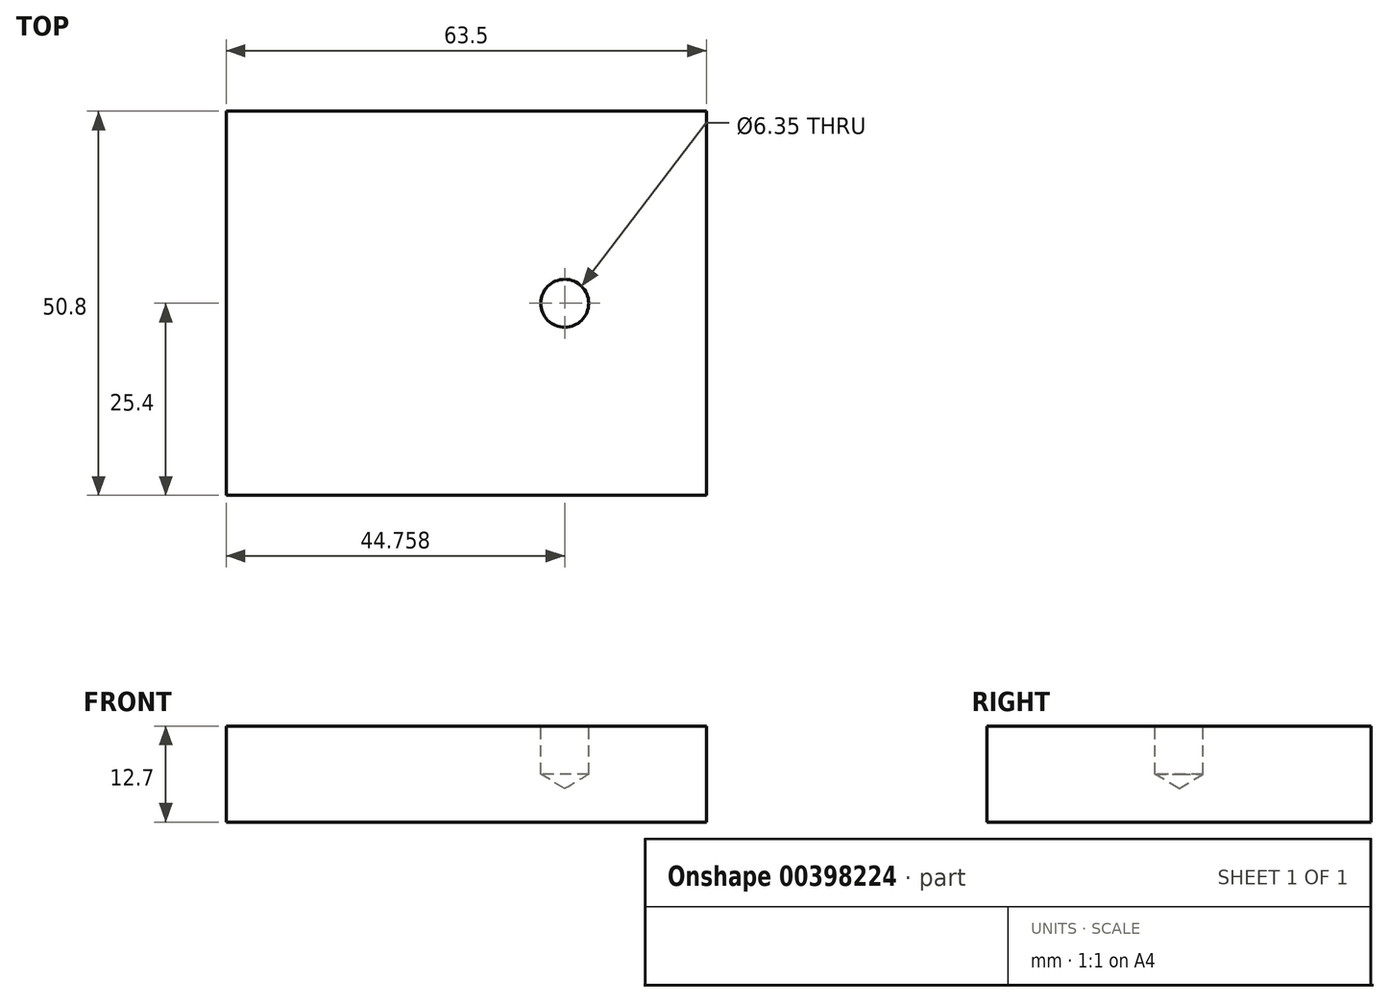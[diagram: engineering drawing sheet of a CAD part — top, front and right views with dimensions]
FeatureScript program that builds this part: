
annotation { "Feature Type Name" : "Feature", "Feature Type Description" : "" }
export const myFeature = defineFeature(function(context is Context, id is Id, definition is map)
    precondition{}
    {
        {
            var Q0;
            Q0=qCreatedBy(makeId("Top.planeOp"),FACE);
            var sketch = newSketch(context, id + "F0", { "sketchPlane" : qUnion([Q0])});
            skLineSegment(sketch, "E0.bottom", {"start": v(-31.75, 25.4) * mm, "end": v(31.75, 25.4) * mm});
            skLineSegment(sketch, "E0.top", {"start": v(-31.75, -25.4) * mm, "end": v(31.75, -25.4) * mm});
            skLineSegment(sketch, "E0.left", {"start": v(-31.75, 25.4) * mm, "end": v(-31.75, -25.4) * mm});
            skLineSegment(sketch, "E0.right", {"start": v(31.75, 25.4) * mm, "end": v(31.75, -25.4) * mm});
            skSolve(sketch);
        }
        {
            var Q0;
            Q0=makeQuery(id+"F0.imprint","IMPRINT",FACE,{"disambiguationData":[TD([[makeQuery(id+"F0.imprint","IMPRINT",EDGE,{"derivedFrom":sQuery(id+"F0.wireOp",EDGE,"E0.bottom")}),-1.0]])]});
            extrude(context, id + "F1", {"entities" : qUnion([Q0]), "depth" : 12.7 * mm});
        }
        {
            var Q0;
            Q0=makeQuery(id+"F1.opExtrude","CAP_FACE",FACE,{"disambiguationData":[OSD([sQuery(id+"F0.wireOp",EDGE,"E0.bottom"),sQuery(id+"F0.wireOp",EDGE,"E0.top"),sQuery(id+"F0.wireOp",EDGE,"E0.left"),sQuery(id+"F0.wireOp",EDGE,"E0.right")])],"isStart":false});
            var sketch = newSketch(context, id + "F2", { "sketchPlane" : qUnion([Q0])});
            skCircle(sketch, "E1", {"center": v(13, 0) * mm, "radius": 3.28 * mm});
            skSolve(sketch);
        }
        {
            var Q0;
            Q0=sQuery(id+"F2.wireOp",VERTEX,"E1.center");
            var Q1;
            Q1=makeQuery(id+"F1.opExtrude","SWEPT_BODY",BODY,{"disambiguationData":[OSD([sQuery(id+"F0.wireOp",EDGE,"E0.bottom"),sQuery(id+"F0.wireOp",EDGE,"E0.top"),sQuery(id+"F0.wireOp",EDGE,"E0.left"),sQuery(id+"F0.wireOp",EDGE,"E0.right")])]});
            hole(context, id + "F3", {"style" : HoleStyle.SIMPLE, "endStyle" : HoleEndStyle.BLIND, "holeDiameter" : 6.35 * mm, "holeDepth" : 6.35 * mm, "isTappedThrough" : true, "tappedDepth" : 12.7 * mm, "tapClearance" : 3, "locations" : qUnion([Q0]), "scope" : qUnion([Q1])});
        }
    });
